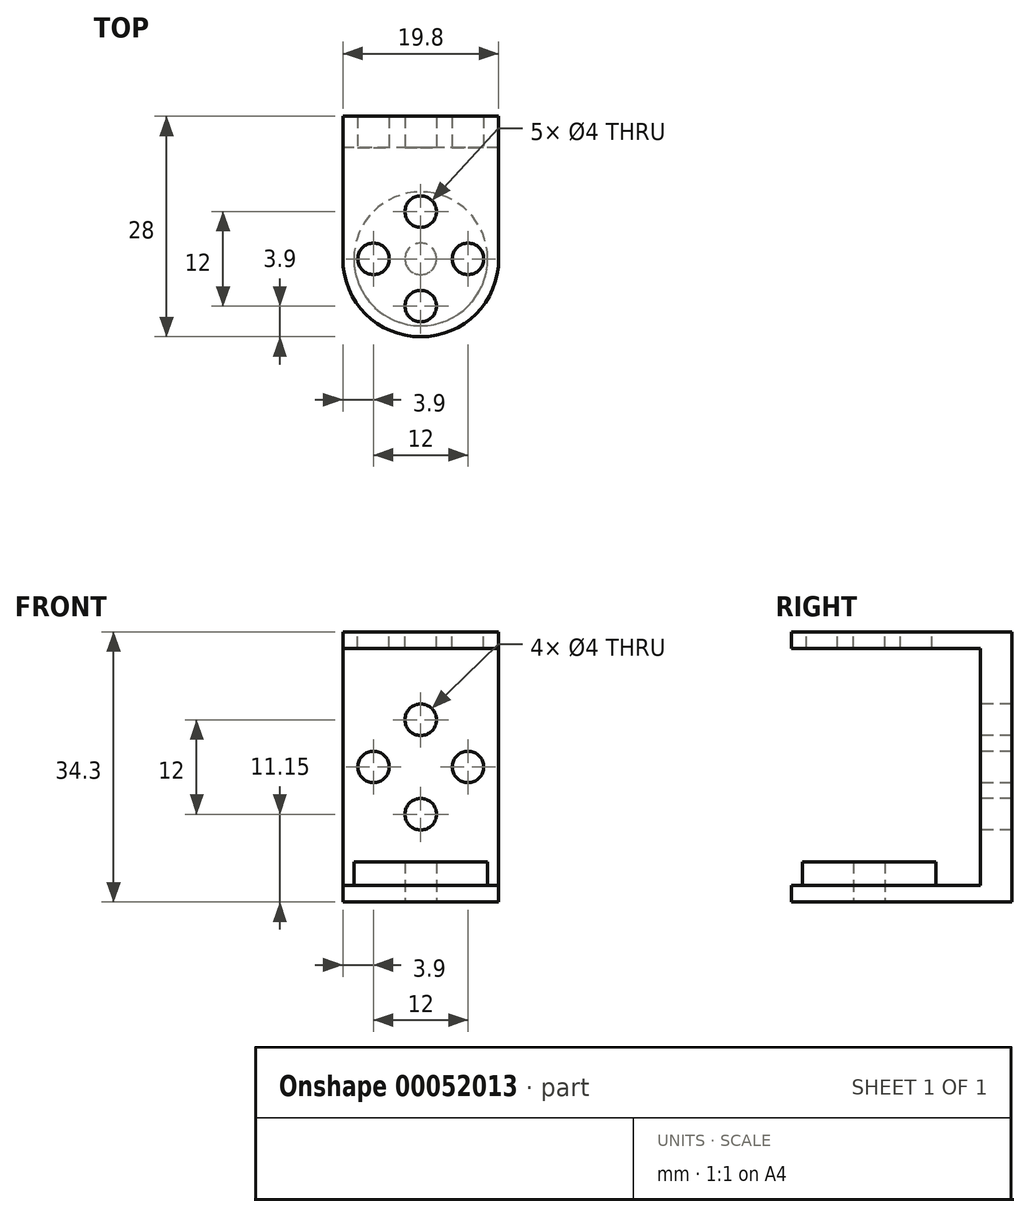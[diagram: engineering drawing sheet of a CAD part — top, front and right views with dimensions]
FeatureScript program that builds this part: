
annotation { "Feature Type Name" : "Feature", "Feature Type Description" : "" }
export const myFeature = defineFeature(function(context is Context, id is Id, definition is map)
    precondition{}
    {
        {
            var Q0;
            Q0=qCreatedBy(makeId("Right.planeOp"),FACE);
            var sketch = newSketch(context, id + "F0", { "sketchPlane" : qUnion([Q0])});
            skLineSegment(sketch, "E0.bottom", {"start": v(0, 17.15) * mm, "end": v(28, 17.15) * mm});
            skLineSegment(sketch, "E0.top", {"start": v(0, 15.05) * mm, "end": v(28, 15.05) * mm});
            skLineSegment(sketch, "E0.left", {"start": v(0, 17.15) * mm, "end": v(0, 15.05) * mm});
            skLineSegment(sketch, "E0.right", {"start": v(28, 17.15) * mm, "end": v(28, 15.05) * mm});
            skLineSegment(sketch, "E1.bottom", {"start": v(28, 15.05) * mm, "end": v(24, 15.05) * mm});
            skLineSegment(sketch, "E1.top", {"start": v(28, -17.15) * mm, "end": v(24, -17.15) * mm});
            skLineSegment(sketch, "E1.left", {"start": v(28, 15.05) * mm, "end": v(28, -17.15) * mm});
            skLineSegment(sketch, "E1.right", {"start": v(24, 15.05) * mm, "end": v(24, -17.15) * mm});
            skLineSegment(sketch, "E2.bottom", {"start": v(28, -17.15) * mm, "end": v(0, -17.15) * mm});
            skLineSegment(sketch, "E2.top", {"start": v(28, -15.05) * mm, "end": v(0, -15.05) * mm});
            skLineSegment(sketch, "E2.left", {"start": v(28, -17.15) * mm, "end": v(28, -15.05) * mm});
            skLineSegment(sketch, "E2.right", {"start": v(0, -17.15) * mm, "end": v(0, -15.05) * mm});
            skSolve(sketch);
        }
        {
            var Q0;
            Q0 = qSketchRegion(id + "F0", true);
            extrude(context, id + "F1", {"entities" : qUnion([Q0]), "endBound" : BoundingType.SYMMETRIC, "depth" : (9.9 * 2) * mm, "offsetDistance" : 25 * mm});
        }
        {
            var Q0;
            Q0=makeQuery(id+"F1.opExtrude","SWEPT_FACE",FACE,{"disambiguationData":[OSD([sQuery(id+"F0.wireOp",EDGE,"E0.bottom")])]});
            var sketch = newSketch(context, id + "F2", { "sketchPlane" : qUnion([Q0])});
            skArc(sketch, "E3", {"start": v(-9.9, 9.9) * mm, "mid": v(0, 0) * mm, "end": v(9.9, 9.9) * mm});
            skLineSegment(sketch, "E4", {"start": v(-9.9, 9.9) * mm, "end": v(-14.9, 9.9) * mm});
            skLineSegment(sketch, "E5", {"start": v(-14.9, 9.9) * mm, "end": v(-14.9, -5) * mm});
            skLineSegment(sketch, "E6", {"start": v(-14.9, -5) * mm, "end": v(14.9, -5) * mm});
            skLineSegment(sketch, "E7", {"start": v(14.9, -5) * mm, "end": v(14.9, 9.9) * mm});
            skLineSegment(sketch, "E8", {"start": v(14.9, 9.9) * mm, "end": v(9.9, 9.9) * mm});
            skCircle(sketch, "E9", {"center": v(0, 15.9) * mm, "radius": 2 * mm});
            skCircle(sketch, "E10", {"center": v(0, 3.9) * mm, "radius": 2 * mm});
            skCircle(sketch, "E11", {"center": v(-6, 9.9) * mm, "radius": 2 * mm});
            skCircle(sketch, "E12", {"center": v(6, 9.9) * mm, "radius": 2 * mm});
            skCircle(sketch, "E13", {"center": v(0, 9.9) * mm, "radius": 6 * mm, "construction": true});
            skSolve(sketch);
        }
        {
            var Q0;
            {var subQ4=sQuery(id+"F2.wireOp",EDGE,"E4");Q0=makeQuery(id+"F2.imprint","IMPRINT",FACE,{"disambiguationData":[TD([[makeQuery(id+"F2.imprint","IMPRINT",EDGE,{"derivedFrom":subQ4}),1.0]])]});}
            var Q1;
            {var subQ0=sQuery(id+"F2.wireOp",EDGE,"E3");var subQ1=sQuery(id+"F0.wireOp",EDGE,"E0.bottom");var subQ2=makeQuery(id+"F1.opExtrude","CAP_EDGE",EDGE,{"disambiguationData":[OSD([subQ1])],"isStart":true});var subQ3=makeQuery(id+"F2.imprint","INTERSECT",VERTEX,{"derivedFrom":[subQ2,subQ0,sQuery(id+"F2.wireOp",EDGE,"E4")]});Q1=makeQuery(id+"F2.imprint","IMPRINT",FACE,{"disambiguationData":[TD([[makeQuery(id+"F2.imprint","IMPRINT",EDGE,{"disambiguationData":[TD([[subQ3,-1.0]])],"derivedFrom":subQ0}),-1.0]])]});}
            var Q2;
            {var subQ0=sQuery(id+"F2.wireOp",EDGE,"E3");var subQ1=sQuery(id+"F0.wireOp",EDGE,"E0.bottom");var subQ2=makeQuery(id+"F1.opExtrude","CAP_EDGE",EDGE,{"disambiguationData":[OSD([subQ1])],"isStart":false});var subQ3=makeQuery(id+"F2.imprint","INTERSECT",VERTEX,{"derivedFrom":[subQ2,subQ0,sQuery(id+"F2.wireOp",EDGE,"E8")]});Q2=makeQuery(id+"F2.imprint","IMPRINT",FACE,{"disambiguationData":[TD([[makeQuery(id+"F2.imprint","IMPRINT",EDGE,{"disambiguationData":[TD([[subQ3,1.0]])],"derivedFrom":subQ0}),-1.0]])]});}
            extrude(context, id + "F3", {"entities" : qUnion([Q0, Q1, Q2]), "operationType" : NewBodyOperationType.REMOVE, "endBound" : BoundingType.THROUGH_ALL, "oppositeDirection" : true, "depth" : 25 * mm, "offsetDistance" : 25 * mm});
        }
        {
            var Q0;
            Q0=makeQuery(id+"F2.imprint","IMPRINT",FACE,{"disambiguationData":[TD([[makeQuery(id+"F2.imprint","IMPRINT",EDGE,{"derivedFrom":sQuery(id+"F2.wireOp",EDGE,"E11")}),1.0]])]});
            var Q1;
            Q1=makeQuery(id+"F2.imprint","IMPRINT",FACE,{"disambiguationData":[TD([[makeQuery(id+"F2.imprint","IMPRINT",EDGE,{"derivedFrom":sQuery(id+"F2.wireOp",EDGE,"E9")}),1.0]])]});
            var Q2;
            Q2=makeQuery(id+"F2.imprint","IMPRINT",FACE,{"disambiguationData":[TD([[makeQuery(id+"F2.imprint","IMPRINT",EDGE,{"derivedFrom":sQuery(id+"F2.wireOp",EDGE,"E12")}),1.0]])]});
            var Q3;
            Q3=makeQuery(id+"F2.imprint","IMPRINT",FACE,{"disambiguationData":[TD([[makeQuery(id+"F2.imprint","IMPRINT",EDGE,{"derivedFrom":sQuery(id+"F2.wireOp",EDGE,"E10")}),1.0]])]});
            extrude(context, id + "F4", {"entities" : qUnion([Q0, Q1, Q2, Q3]), "operationType" : NewBodyOperationType.REMOVE, "endBound" : BoundingType.UP_TO_NEXT, "oppositeDirection" : true, "depth" : 25 * mm, "offsetDistance" : 25 * mm});
        }
        {
            var Q0;
            Q0=makeQuery(id+"F1.opExtrude","SWEPT_FACE",FACE,{"disambiguationData":[OSD([sQuery(id+"F0.wireOp",EDGE,"E2.top")])]});
            var sketch = newSketch(context, id + "F5", { "sketchPlane" : qUnion([Q0])});
            skCircle(sketch, "E14", {"center": v(0, 9.9) * mm, "radius": 8.5 * mm});
            skCircle(sketch, "E15", {"center": v(0, 9.9) * mm, "radius": 2 * mm});
            skSolve(sketch);
        }
        {
            var Q0;
            Q0=makeQuery(id+"F5.imprint","IMPRINT",FACE,{"disambiguationData":[TD([[makeQuery(id+"F5.imprint","IMPRINT",EDGE,{"derivedFrom":sQuery(id+"F5.wireOp",EDGE,"E14")}),1.0]])]});
            extrude(context, id + "F6", {"entities" : qUnion([Q0]), "operationType" : NewBodyOperationType.ADD, "depth" : 3 * mm, "offsetDistance" : 25 * mm});
        }
        {
            var Q0;
            Q0=makeQuery(id+"F5.imprint","IMPRINT",FACE,{"disambiguationData":[TD([[makeQuery(id+"F5.imprint","IMPRINT",EDGE,{"derivedFrom":sQuery(id+"F5.wireOp",EDGE,"E15")}),1.0]])]});
            extrude(context, id + "F7", {"entities" : qUnion([Q0]), "operationType" : NewBodyOperationType.REMOVE, "endBound" : BoundingType.THROUGH_ALL, "oppositeDirection" : true, "depth" : 25 * mm, "offsetDistance" : 25 * mm});
        }
        {
            var Q0;
            Q0=makeQuery(id+"F1.opExtrude","SWEPT_FACE",FACE,{"disambiguationData":[OSD([sQuery(id+"F0.wireOp",EDGE,"E1.right")])]});
            var sketch = newSketch(context, id + "F8", { "sketchPlane" : qUnion([Q0])});
            skCircle(sketch, "E16", {"center": v(0, 0) * mm, "radius": 6 * mm, "construction": true});
            skCircle(sketch, "E17", {"center": v(0, 6) * mm, "radius": 2 * mm});
            skCircle(sketch, "E18", {"center": v(6, 0) * mm, "radius": 2 * mm});
            skCircle(sketch, "E19", {"center": v(0, -6) * mm, "radius": 2 * mm});
            skCircle(sketch, "E20", {"center": v(-6, 0) * mm, "radius": 2 * mm});
            skSolve(sketch);
        }
        {
            var Q0;
            Q0 = qSketchRegion(id + "F8", true);
            extrude(context, id + "F9", {"entities" : qUnion([Q0]), "operationType" : NewBodyOperationType.REMOVE, "endBound" : BoundingType.THROUGH_ALL, "oppositeDirection" : true, "depth" : 25 * mm, "offsetDistance" : 25 * mm});
        }
    });
